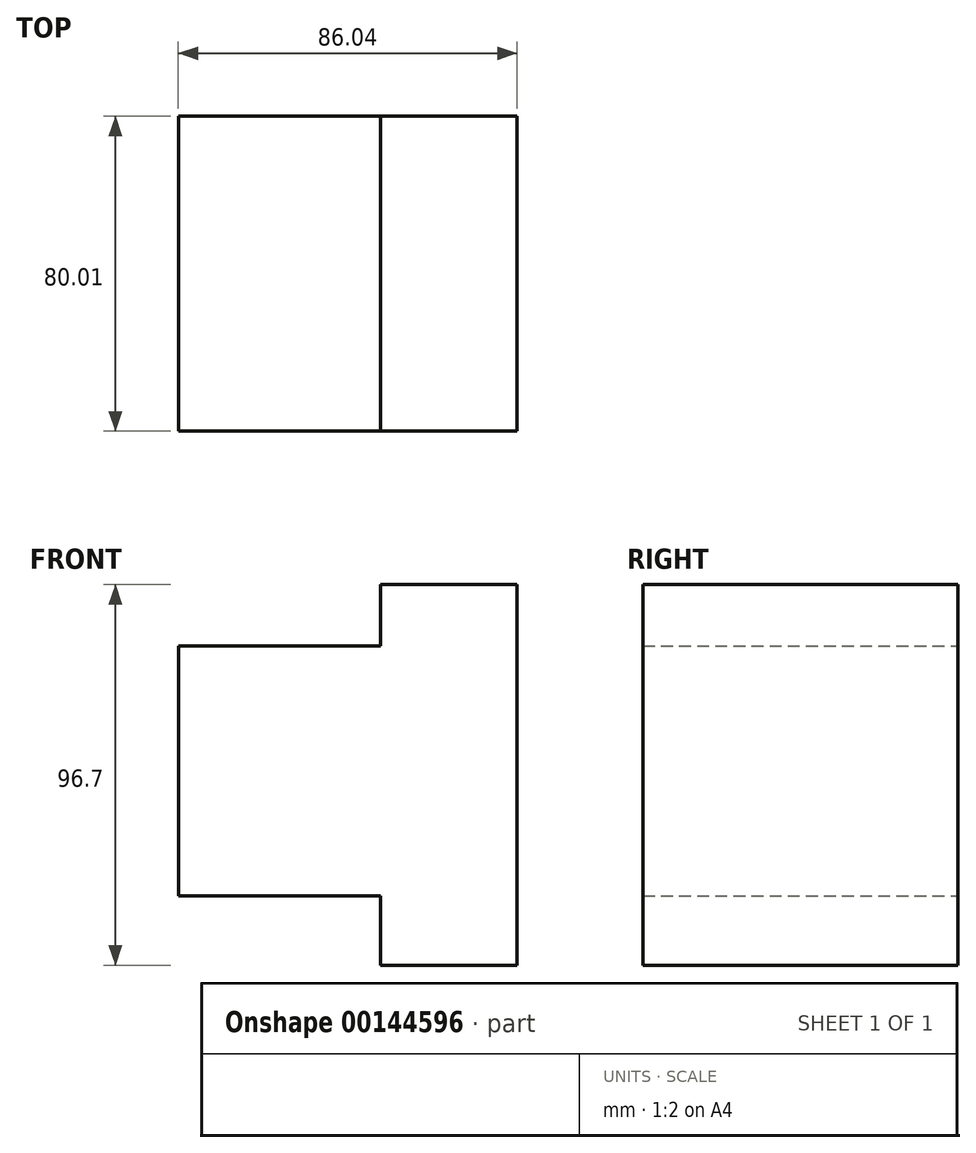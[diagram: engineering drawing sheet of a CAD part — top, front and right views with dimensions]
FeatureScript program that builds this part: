
annotation { "Feature Type Name" : "Feature", "Feature Type Description" : "" }
export const myFeature = defineFeature(function(context is Context, id is Id, definition is map)
    precondition{}
    {
        {
            var Q0;
            Q0=qCreatedBy(makeId("Front.planeOp"),FACE);
            var sketch = newSketch(context, id + "F0", { "sketchPlane" : qUnion([Q0])});
            skLineSegment(sketch, "E0.bottom", {"start": v(34.65, 31.75) * mm, "end": v(-34.65, 31.75) * mm});
            skLineSegment(sketch, "E0.top", {"start": v(34.65, -31.75) * mm, "end": v(-34.65, -31.75) * mm});
            skLineSegment(sketch, "E0.left", {"start": v(34.65, 31.75) * mm, "end": v(34.65, -31.75) * mm});
            skLineSegment(sketch, "E0.right", {"start": v(-34.65, 31.75) * mm, "end": v(-34.65, -31.75) * mm});
            skPoint(sketch, "E0.middle", {"position": v(0, 0) * mm});
            skSolve(sketch);
        }
        {
            var Q0;
            Q0=makeQuery(id+"F0.imprint","IMPRINT",FACE,{"disambiguationData":[TD([[makeQuery(id+"F0.imprint","IMPRINT",EDGE,{"derivedFrom":sQuery(id+"F0.wireOp",EDGE,"E0.bottom")}),1.0]])]});
            var sketch = newSketch(context, id + "F1", { "sketchPlane" : qUnion([Q0])});
            skLineSegment(sketch, "E1.bottom", {"start": v(16.7, 47.36) * mm, "end": v(51.4, 47.36) * mm});
            skLineSegment(sketch, "E1.top", {"start": v(16.7, -49.34) * mm, "end": v(51.4, -49.34) * mm});
            skLineSegment(sketch, "E1.left", {"start": v(16.7, 47.36) * mm, "end": v(16.7, -49.34) * mm});
            skLineSegment(sketch, "E1.right", {"start": v(51.4, 47.36) * mm, "end": v(51.4, -49.34) * mm});
            skSolve(sketch);
        }
        {
            var Q0;
            Q0 = qSketchRegion(id + "F1", true);
            var Q1;
            {var subQ5=makeQuery(id+"F0.imprint","IMPRINT",EDGE,{"derivedFrom":sQuery(id+"F0.wireOp",EDGE,"E0.right")});Q1=makeQuery(id+"F1.imprint","IMPRINT",FACE,{"disambiguationData":[TD([[makeQuery(id+"F1.imprint","IMPRINT",EDGE,{"derivedFrom":subQ5}),1.0]])]});}
            extrude(context, id + "F2", {"entities" : qUnion([Q0, Q1]), "depth" : 80 * mm});
        }
    });
